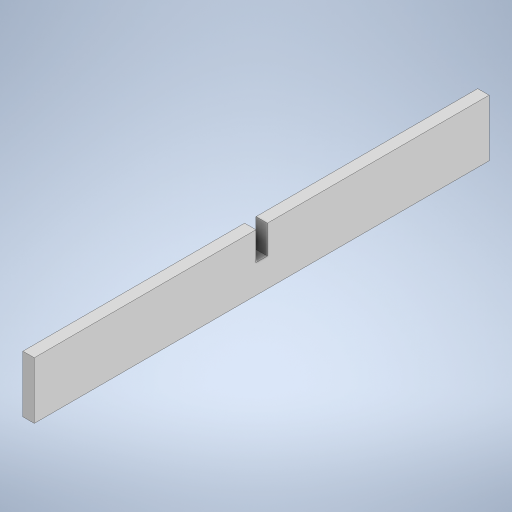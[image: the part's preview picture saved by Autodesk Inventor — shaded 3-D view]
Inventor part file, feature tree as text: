
AUTODESK INVENTOR PART (.ipt)
format: ipt  version: 2024.3 (Build 283343000, 343)  size: 231,936 bytes
history: native  units: mm
features: extrude x2, sketch x2
ambient origin geometry x8: Origin, YZ Plane, XZ Plane, XY Plane, X Axis, Y Axis, Z Axis, Center Point
bodies: Solid1 (feature_tree)
feature tree (4):
  extrude  "Extrusion1"  Depth=25.0mm
  extrude  "Extrusion2"  Depth=5.0mm
  sketch  "Sketch1"  dims[d0=200.0mm d1=25.0mm]
  sketch  "Sketch2"  dims[d2=5.0mm d3=0.0mm d4=5.0mm d5=5.0mm d6=0.0mm]
